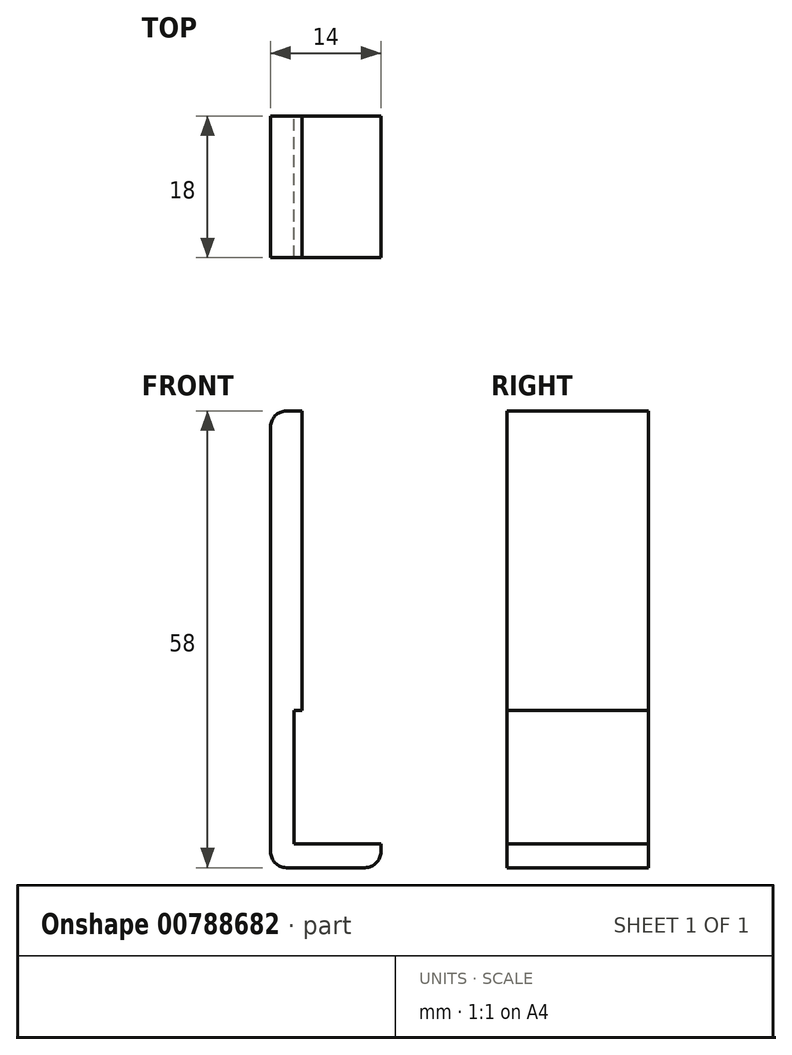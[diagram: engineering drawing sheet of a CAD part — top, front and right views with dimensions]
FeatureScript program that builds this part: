
annotation { "Feature Type Name" : "Feature", "Feature Type Description" : "" }
export const myFeature = defineFeature(function(context is Context, id is Id, definition is map)
    precondition{}
    {
        {
            var Q0;
            Q0=qCreatedBy(makeId("Front.planeOp"),FACE);
            var sketch = newSketch(context, id + "F0", { "sketchPlane" : qUnion([Q0])});
            skLineSegment(sketch, "E0", {"start": v(0, 0) * mm, "end": v(10, 0) * mm});
            skLineSegment(sketch, "E1", {"start": v(10, 0) * mm, "end": v(10, -3) * mm});
            skLineSegment(sketch, "E2", {"start": v(10, -3) * mm, "end": v(-4, -3) * mm});
            skLineSegment(sketch, "E3", {"start": v(-4, -3) * mm, "end": v(-4, 55) * mm});
            skLineSegment(sketch, "E4", {"start": v(-4, 55) * mm, "end": v(0, 55) * mm});
            skLineSegment(sketch, "E5", {"start": v(0, 55) * mm, "end": v(0, 0) * mm});
            skSolve(sketch);
        }
        {
            var Q0;
            Q0=makeQuery(id+"F0.imprint","IMPRINT",FACE,{"disambiguationData":[TD([[makeQuery(id+"F0.imprint","IMPRINT",EDGE,{"derivedFrom":sQuery(id+"F0.wireOp",EDGE,"E0")}),-1.0]])]});
            extrude(context, id + "F1", {"entities" : qUnion([Q0]), "endBound" : BoundingType.SYMMETRIC, "depth" : 18 * mm, "offsetDistance" : 25 * mm});
        }
        {
            var Q0;
            Q0=makeQuery(id+"F1.opExtrude","SWEPT_EDGE",EDGE,{"disambiguationData":[OSD([sQuery(id+"F0.wireOp",EDGE,"E3"),sQuery(id+"F0.wireOp",EDGE,"E4")])]});
            var Q1;
            Q1=makeQuery(id+"F1.opExtrude","SWEPT_EDGE",EDGE,{"disambiguationData":[OSD([sQuery(id+"F0.wireOp",EDGE,"E2"),sQuery(id+"F0.wireOp",EDGE,"E3")])]});
            var Q2;
            Q2=makeQuery(id+"F1.opExtrude","SWEPT_EDGE",EDGE,{"disambiguationData":[OSD([sQuery(id+"F0.wireOp",EDGE,"E1"),sQuery(id+"F0.wireOp",EDGE,"E2")])]});
            fillet(context, id + "F2", {"entities" : qUnion([Q0, Q1, Q2]), "radius" : 2 * mm, "tangentPropagation" : true, "allowEdgeOverflow" : false});
        }
        {
            var Q0;
            Q0=makeQuery(id+"F1.opExtrude","SWEPT_FACE",FACE,{"disambiguationData":[OSD([sQuery(id+"F0.wireOp",EDGE,"E5")])]});
            var sketch = newSketch(context, id + "F3", { "sketchPlane" : qUnion([Q0])});
            skLineSegment(sketch, "E6.bottom", {"start": v(-9, 0) * mm, "end": v(9, 0) * mm});
            skLineSegment(sketch, "E6.top", {"start": v(-9, 17) * mm, "end": v(9, 17) * mm});
            skLineSegment(sketch, "E6.left", {"start": v(-9, 0) * mm, "end": v(-9, 17) * mm});
            skLineSegment(sketch, "E6.right", {"start": v(9, 0) * mm, "end": v(9, 17) * mm});
            skSolve(sketch);
        }
        {
            var Q0;
            Q0=makeQuery(id+"F3.imprint","IMPRINT",FACE,{"disambiguationData":[TD([[makeQuery(id+"F3.imprint","IMPRINT",EDGE,{"derivedFrom":sQuery(id+"F3.wireOp",EDGE,"E6.bottom")}),1.0]])]});
            extrude(context, id + "F4", {"entities" : qUnion([Q0]), "operationType" : NewBodyOperationType.REMOVE, "oppositeDirection" : true, "depth" : 1 * mm, "offsetDistance" : 25 * mm});
        }
    });
